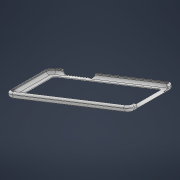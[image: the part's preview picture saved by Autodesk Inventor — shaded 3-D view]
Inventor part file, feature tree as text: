
AUTODESK INVENTOR PART (.ipt)
format: ipt  version: 2021 (Build 250183000, 183)  size: 1,206,272 bytes
history: native  units: mm
features: other x7, sketch x5, extrude x4, fillet x3, plane x2, thicken_offset x1, chamfer x1, surface_op x1
ambient origin geometry x8: Origin, YZ Plane, XZ Plane, XY Plane, X Axis, Y Axis, Z Axis, Center Point
bodies: Solid1 (feature_tree), Solid2 (feature_tree)
feature tree (24):
  extrude  "Extrusion1"  Depth=137.5mm
  fillet  "Fillet1"  [1 undecoded]
  fillet  "Fillet2"  Radius=9.9mm
  fillet  "Fillet3"  Radius=1.46mm
  thicken_offset  "Thicken1"
  chamfer  "Chamfer2"  [1 undecoded]
  extrude  "Extrusion2"  Depth=10.0mm TaperAngle=0.0deg
  plane  "Work Plane1"
  plane  "Work Plane2"
  other  "Ruled Surface6"
  surface_op  "Sculpt1"
  extrude  "Extrusion3"  Depth=10.0mm TaperAngle=0.0deg
  extrude  "Extrusion5"  Depth=2.0mm
  sketch  "Sketch1"  dims[d0=208.4mm d1=137.5mm d3=0.0mm d4=9.9mm d7=1.46mm d8=0.8mm d18=0.0mm d19=0.0mm]
  sketch  "Sketch3"  dims[d20=53.5mm d22=10.0mm d23=0.0mm]
  sketch  "Sketch4"  dims[d28=5.9mm d29=10.0mm d30=0.0mm]
  sketch  "Sketch5"  dims[d31=5.9mm d32=2.0mm d33=2.0mm d34=3.5mm d35=10.0mm d36=3.5mm d37=10.0mm d38=5.0mm d39=0.0mm d40=5.0mm d41=10.0mm d42=8.0mm d43=8.0mm d44=8.0mm d45=8.0mm d46=5.9mm d47=24.5mm d48=19.0mm d49=19.0mm d53=0.5mm d54=2.0mm d55=45.0deg d87=10.0mm d88=5.585054mm d89=10.0mm d90=0.0mm d91=10.0mm d92=45.0deg]
  other  "Srf7"
  other  "Ruled Surface7"
  other  "Srf8"
  sketch  "3D Sketch9"
  other  "Ruled Surface8"
  other  "Srf9"
  other  "3D Intersection3"
note: 2 required parameter values undecoded (feature->parameter linkage not recoverable at this tier; creation-order binding heuristic only, values carry confidence <= 0.55)
